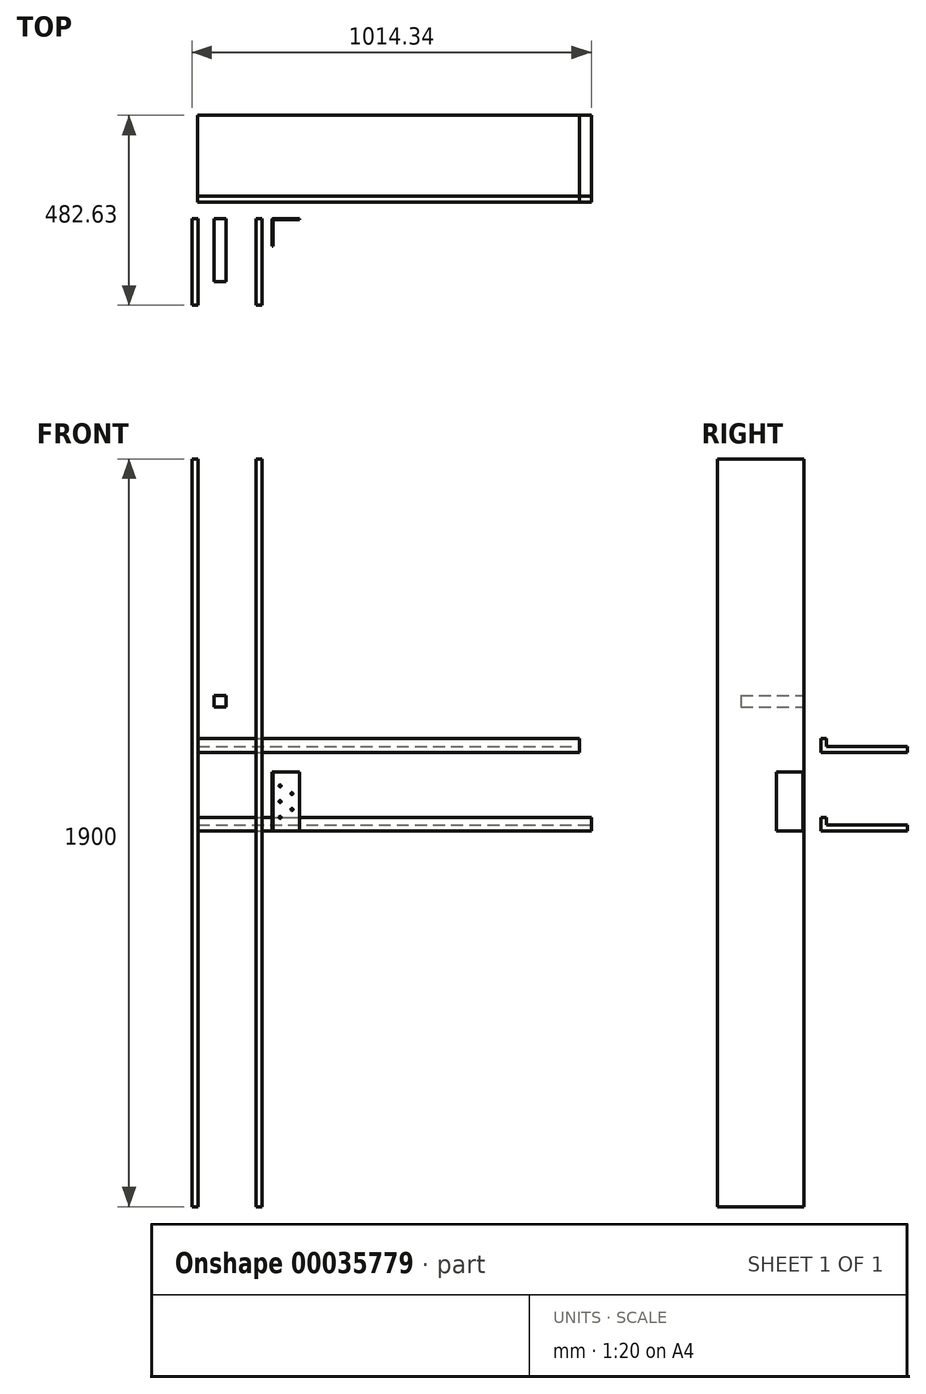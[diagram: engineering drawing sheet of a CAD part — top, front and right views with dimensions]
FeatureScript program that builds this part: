
annotation { "Feature Type Name" : "Feature", "Feature Type Description" : "" }
export const myFeature = defineFeature(function(context is Context, id is Id, definition is map)
    precondition{}
    {
        {
            var Q0;
            Q0=qCreatedBy(makeId("Front.planeOp"),FACE);
            var sketch = newSketch(context, id + "F0", { "sketchPlane" : qUnion([Q0])});
            skLineSegment(sketch, "E0.bottom", {"start": v(-88.68, 945.75) * mm, "end": v(-73.68, 945.75) * mm});
            skLineSegment(sketch, "E0.top", {"start": v(-88.68, -954.25) * mm, "end": v(-73.68, -954.25) * mm});
            skLineSegment(sketch, "E0.left", {"start": v(-88.68, 945.75) * mm, "end": v(-88.68, -954.25) * mm});
            skLineSegment(sketch, "E0.right", {"start": v(-73.68, 945.75) * mm, "end": v(-73.68, -954.25) * mm});
            skSolve(sketch);
        }
        {
            var Q0;
            Q0=makeQuery(id+"F0.imprint","IMPRINT",FACE,{"disambiguationData":[TD([[makeQuery(id+"F0.imprint","IMPRINT",EDGE,{"derivedFrom":sQuery(id+"F0.wireOp",EDGE,"E0.bottom")}),-1.0]])]});
            extrude(context, id + "F1", {"entities" : qUnion([Q0]), "depth" : 220 * mm});
        }
        {
            var Q0;
            Q0=qCreatedBy(makeId("Front.planeOp"),FACE);
            var sketch = newSketch(context, id + "F2", { "sketchPlane" : qUnion([Q0])});
            skLineSegment(sketch, "E1.bottom", {"start": v(-32.93, 344.88) * mm, "end": v(-2.93, 344.88) * mm});
            skLineSegment(sketch, "E1.top", {"start": v(-32.93, 314.88) * mm, "end": v(-2.93, 314.88) * mm});
            skLineSegment(sketch, "E1.left", {"start": v(-32.93, 344.88) * mm, "end": v(-32.93, 314.88) * mm});
            skLineSegment(sketch, "E1.right", {"start": v(-2.93, 344.88) * mm, "end": v(-2.93, 314.88) * mm});
            skSolve(sketch);
        }
        {
            var Q0;
            Q0=makeQuery(id+"F2.imprint","IMPRINT",FACE,{"disambiguationData":[TD([[makeQuery(id+"F2.imprint","IMPRINT",EDGE,{"derivedFrom":sQuery(id+"F2.wireOp",EDGE,"E1.bottom")}),-1.0]])]});
            extrude(context, id + "F3", {"entities" : qUnion([Q0]), "depth" : 160 * mm});
        }
        {
            var Q0;
            Q0=qCreatedBy(makeId("Top.planeOp"),FACE);
            var sketch = newSketch(context, id + "F4", { "sketchPlane" : qUnion([Q0])});
            skLineSegment(sketch, "E2.bottom", {"start": v(-74.34, 262.63) * mm, "end": v(925.66, 262.63) * mm});
            skLineSegment(sketch, "E2.top", {"start": v(-74.34, 42.63) * mm, "end": v(925.66, 42.63) * mm});
            skLineSegment(sketch, "E2.left", {"start": v(-74.34, 262.63) * mm, "end": v(-74.34, 42.63) * mm});
            skLineSegment(sketch, "E2.right", {"start": v(925.66, 262.63) * mm, "end": v(925.66, 42.63) * mm});
            skSolve(sketch);
        }
        {
            var Q0;
            Q0=makeQuery(id+"F4.imprint","IMPRINT",FACE,{"disambiguationData":[TD([[makeQuery(id+"F4.imprint","IMPRINT",EDGE,{"derivedFrom":sQuery(id+"F4.wireOp",EDGE,"E2.bottom")}),-1.0]])]});
            extrude(context, id + "F5", {"entities" : qUnion([Q0]), "depth" : 15 * mm});
        }
        {
            var Q0;
            Q0=makeQuery(id+"F5.opExtrude","CAP_FACE",FACE,{"disambiguationData":[OSD([sQuery(id+"F4.wireOp",EDGE,"E2.bottom"),sQuery(id+"F4.wireOp",EDGE,"E2.top"),sQuery(id+"F4.wireOp",EDGE,"E2.left"),sQuery(id+"F4.wireOp",EDGE,"E2.right")])],"isStart":false});
            var sketch = newSketch(context, id + "F6", { "sketchPlane" : qUnion([Q0])});
            skLineSegment(sketch, "E3", {"start": v(-74.34, 57.63) * mm, "end": v(925.66, 57.63) * mm});
            skSolve(sketch);
        }
        {
            var Q0;
            {var subQ1=sQuery(id+"F6.wireOp",EDGE,"E3");Q0=makeQuery(id+"F6.imprint","IMPRINT",FACE,{"disambiguationData":[TD([[makeQuery(id+"F6.imprint","IMPRINT",EDGE,{"derivedFrom":subQ1}),-1.0]])]});}
            extrude(context, id + "F7", {"entities" : qUnion([Q0]), "operationType" : NewBodyOperationType.ADD, "depth" : 20 * mm});
        }
        {
            var Q0;
            Q0=qCreatedBy(makeId("Top.planeOp"),FACE);
            var sketch = newSketch(context, id + "F8", { "sketchPlane" : qUnion([Q0])});
            skLineSegment(sketch, "E4", {"start": v(184.84, 0) * mm, "end": v(115.84, 0) * mm});
            skLineSegment(sketch, "E5", {"start": v(114.84, -1) * mm, "end": v(114.84, -70) * mm});
            skLineSegment(sketch, "E6", {"start": v(114.84, -70) * mm, "end": v(116.84, -70) * mm});
            skLineSegment(sketch, "E7", {"start": v(116.84, -70) * mm, "end": v(116.84, -3) * mm});
            skLineSegment(sketch, "E8", {"start": v(117.84, -2) * mm, "end": v(184.84, -2) * mm});
            skLineSegment(sketch, "E9", {"start": v(184.84, -2) * mm, "end": v(184.84, 0) * mm});
            skPoint(sketch, "E10.visualSharp", {"position": v(116.84, -2) * mm});
            skArc(sketch, "E10.filletArc", {"start": v(117.84, -2) * mm, "mid": v(117.13, -2.3) * mm, "end": v(116.84, -3) * mm});
            skPoint(sketch, "E11.visualSharp", {"position": v(114.84, 0) * mm});
            skArc(sketch, "E11.filletArc", {"start": v(115.84, 0) * mm, "mid": v(115.13, -0.3) * mm, "end": v(114.84, -1) * mm});
            skSolve(sketch);
        }
        {
            var Q0;
            Q0=makeQuery(id+"F8.imprint","IMPRINT",FACE,{"disambiguationData":[TD([[makeQuery(id+"F8.imprint","IMPRINT",EDGE,{"derivedFrom":sQuery(id+"F8.wireOp",EDGE,"E4")}),1.0]])]});
            extrude(context, id + "F9", {"entities" : qUnion([Q0]), "depth" : 150 * mm});
        }
        {
            var Q0;
            Q0=makeQuery(id+"F9.opExtrude","SWEPT_FACE",FACE,{"disambiguationData":[OSD([sQuery(id+"F8.wireOp",EDGE,"E8")])]});
            var sketch = newSketch(context, id + "F10", { "sketchPlane" : qUnion([Q0])});
            skCircle(sketch, "E12", {"center": v(134.84, 115) * mm, "radius": 2.5 * mm});
            skCircle(sketch, "E13", {"center": v(164.84, 95) * mm, "radius": 2.5 * mm});
            skCircle(sketch, "E14", {"center": v(134.84, 75) * mm, "radius": 2.5 * mm});
            skCircle(sketch, "E15", {"center": v(164.84, 55) * mm, "radius": 2.5 * mm});
            skCircle(sketch, "E16", {"center": v(134.84, 35) * mm, "radius": 2.5 * mm});
            skSolve(sketch);
        }
        {
            var Q0;
            Q0=sQuery(id+"F10.wireOp",VERTEX,"E12.center");
            var Q1;
            Q1=sQuery(id+"F10.wireOp",VERTEX,"E13.center");
            var Q2;
            Q2=sQuery(id+"F10.wireOp",VERTEX,"E14.center");
            var Q3;
            Q3=sQuery(id+"F10.wireOp",VERTEX,"E15.center");
            var Q4;
            Q4=sQuery(id+"F10.wireOp",VERTEX,"E16.center");
            var Q5;
            Q5=makeQuery(id+"F9.opExtrude","SWEPT_BODY",BODY,{"disambiguationData":[OSD([sQuery(id+"F8.wireOp",EDGE,"E4"),sQuery(id+"F8.wireOp",EDGE,"E5"),sQuery(id+"F8.wireOp",EDGE,"E6"),sQuery(id+"F8.wireOp",EDGE,"E7"),sQuery(id+"F8.wireOp",EDGE,"E8"),sQuery(id+"F8.wireOp",EDGE,"E9"),sQuery(id+"F8.wireOp",EDGE,"E10.filletArc"),sQuery(id+"F8.wireOp",EDGE,"E11.filletArc")])]});
            hole(context, id + "F11", {"style" : HoleStyle.SIMPLE, "holeDiameter" : 5 * mm, "endStyle" : HoleEndStyle.THROUGH, "locations" : qUnion([Q0, Q1, Q2, Q3, Q4]), "scope" : qUnion([Q5])});
        }
        {
            var Q0;
            Q0=makeQuery(id+"F5.opExtrude","SWEPT_BODY",BODY,{"disambiguationData":[OSD([sQuery(id+"F4.wireOp",EDGE,"E2.bottom"),sQuery(id+"F4.wireOp",EDGE,"E2.top"),sQuery(id+"F4.wireOp",EDGE,"E2.left"),sQuery(id+"F4.wireOp",EDGE,"E2.right")])]});
            transform(context, id + "F12", {"entities" : qUnion([Q0]), "transformType" : TransformType.TRANSLATION_3D, "dx" : 0 * mm, "dy" : 0 * mm, "dz" : 200 * mm, "makeCopy" : true});
        }
        {
            var Q0;
            {var subQ0=sQuery(id+"F4.wireOp",EDGE,"E2.right");Q0=makeQuery(id+"F12.opPattern","COPY",FACE,{"derivedFrom":makeQuery(id+"F7.boolean.opBoolean","MERGE",FACE,{"derivedFrom":[makeQuery(id+"F5.opExtrude","SWEPT_FACE",FACE,{"disambiguationData":[OSD([subQ0])]}),makeQuery(id+"F7.opExtrude","SWEPT_FACE",FACE,{"disambiguationData":[OSD([subQ0])]})]}),"instanceName":"1"});}
            extrude(context, id + "F13", {"entities" : qUnion([Q0]), "operationType" : NewBodyOperationType.REMOVE, "oppositeDirection" : true, "depth" : 30 * mm});
        }
        {
            var Q0;
            Q0=makeQuery(id+"F1.opExtrude","SWEPT_BODY",BODY,{"disambiguationData":[OSD([sQuery(id+"F0.wireOp",EDGE,"E0.bottom"),sQuery(id+"F0.wireOp",EDGE,"E0.top"),sQuery(id+"F0.wireOp",EDGE,"E0.left"),sQuery(id+"F0.wireOp",EDGE,"E0.right")])]});
            var Q1;
            Q1=qCreatedBy(makeId("Right.planeOp"),FACE);
            mirror(context, id + "F14", {"entities" : qUnion([Q0]), "mirrorPlane" : qUnion([Q1])});
        }
    });
